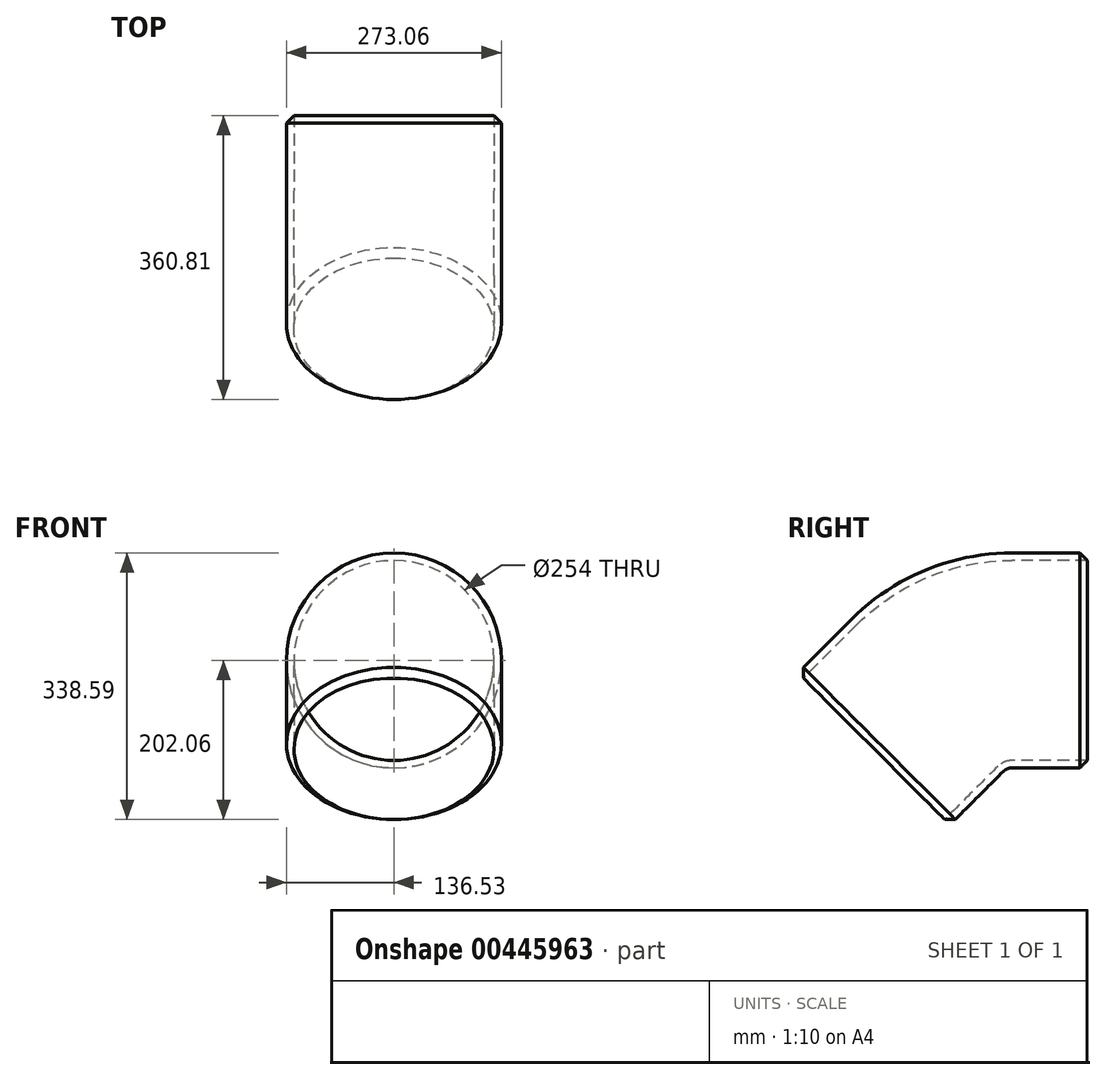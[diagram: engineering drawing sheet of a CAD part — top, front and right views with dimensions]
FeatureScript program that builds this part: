
annotation { "Feature Type Name" : "Feature", "Feature Type Description" : "" }
export const myFeature = defineFeature(function(context is Context, id is Id, definition is map)
    precondition{}
    {
        {
            var Q0;
            Q0=qCreatedBy(makeId("Front.planeOp"),FACE);
            var sketch = newSketch(context, id + "F0", { "sketchPlane" : qUnion([Q0])});
            skCircle(sketch, "E0", {"center": v(0, 0) * mm, "radius": 136.53 * mm});
            skCircle(sketch, "E1", {"center": v(0, 0) * mm, "radius": 127 * mm});
            skSolve(sketch);
        }
        {
            var Q0;
            Q0=qCreatedBy(makeId("Right.planeOp"),FACE);
            var sketch = newSketch(context, id + "F1", { "sketchPlane" : qUnion([Q0])});
            skLineSegment(sketch, "E2", {"start": v(0, 0) * mm, "end": v(-95.62, 0) * mm});
            skLineSegment(sketch, "E3", {"start": v(-203.39, -44.64) * mm, "end": v(-271, -112.25) * mm});
            skPoint(sketch, "E4.visualSharp", {"position": v(-158.75, 0) * mm});
            skArc(sketch, "E4.filletArc", {"start": v(-95.62, 0) * mm, "mid": v(-153.94, -11.6) * mm, "end": v(-203.39, -44.64) * mm});
            skSolve(sketch);
        }
        {
            var Q0;
            Q0 = qSketchRegion(id + "F0", true);
            var Q1;
            Q1 = qConstructionFilter(qBodyType(qCreatedBy(id + "F1" ,EDGE), BodyType.WIRE), ConstructionObject.NO);
            sweep(context, id + "F2", {"profiles" : qUnion([Q0]), "path" : qUnion([Q1])});
        }
        {
            var Q0;
            Q0=makeQuery(id+"F2.opSweep","CAP_EDGE",EDGE,{"disambiguationData":[OSD([sQuery(id+"F0.wireOp",EDGE,"E0"),sQuery(id+"F1.wireOp",VERTEX,"E2.start")])],"isStart":true});
            var Q1;
            Q1=makeQuery(id+"F2.opSweep","CAP_EDGE",EDGE,{"disambiguationData":[OSD([sQuery(id+"F0.wireOp",EDGE,"E0"),sQuery(id+"F1.wireOp",VERTEX,"E3.end")])],"isStart":false});
            chamfer(context, id + "F3", {"entities" : qUnion([Q0, Q1]), "width" : 9.52 * mm, "tangentPropagation" : true});
        }
    });
